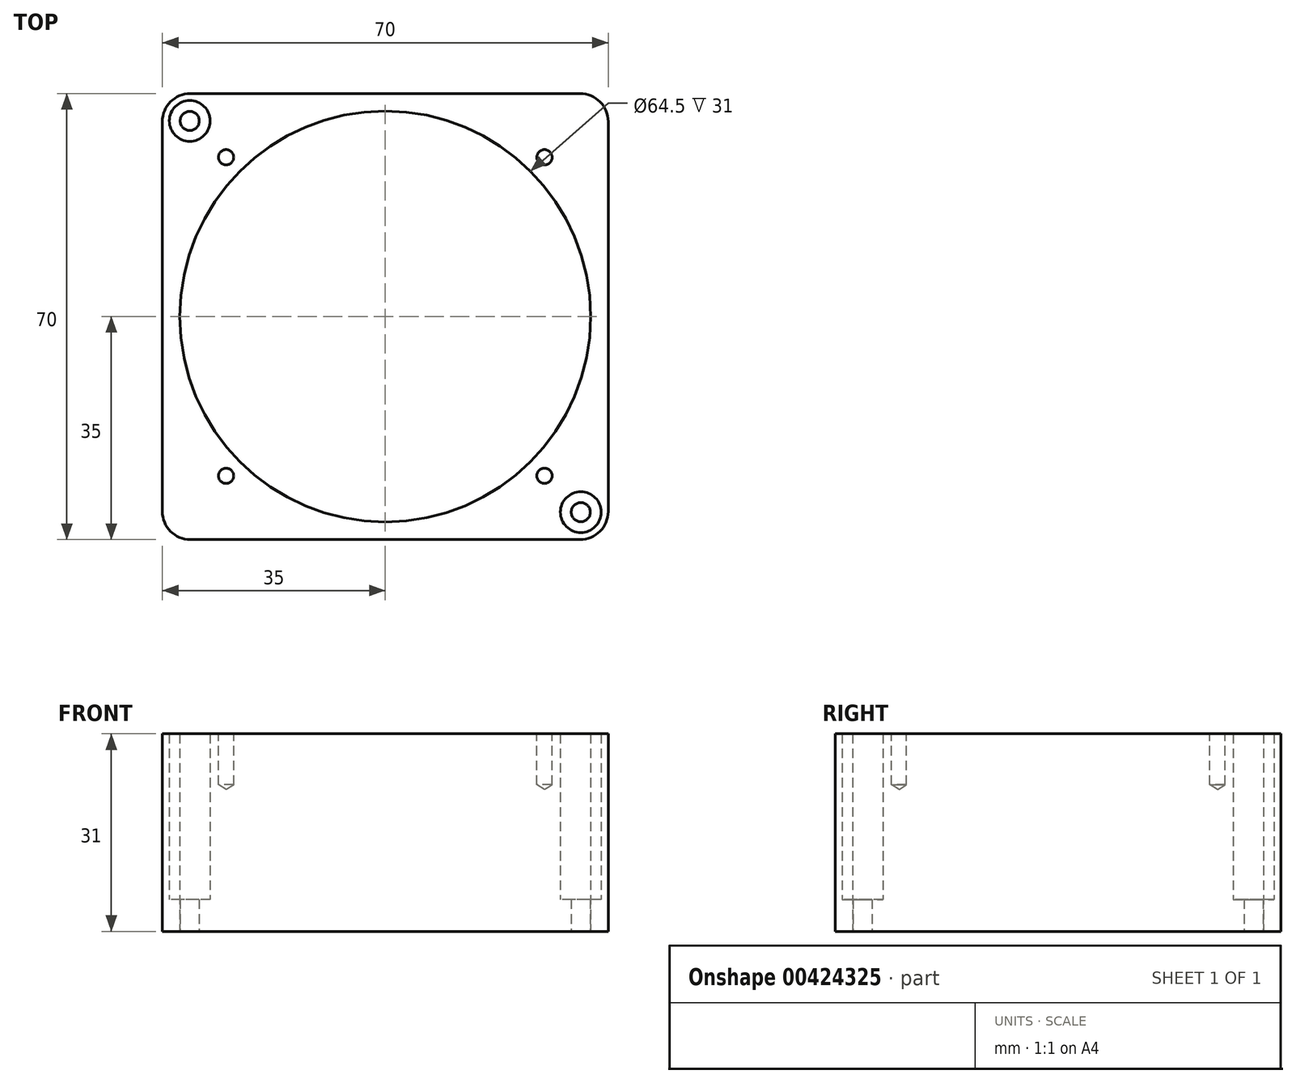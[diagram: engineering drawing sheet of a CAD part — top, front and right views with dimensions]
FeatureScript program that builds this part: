
annotation { "Feature Type Name" : "Feature", "Feature Type Description" : "" }
export const myFeature = defineFeature(function(context is Context, id is Id, definition is map)
    precondition{}
    {
        {
            var Q0;
            Q0=qCreatedBy(makeId("Top.planeOp"),FACE);
            var sketch = newSketch(context, id + "F0", { "sketchPlane" : qUnion([Q0])});
            skLineSegment(sketch, "E0.bottom", {"start": v(35, 35) * mm, "end": v(-35, 35) * mm});
            skLineSegment(sketch, "E0.top", {"start": v(35, -35) * mm, "end": v(-35, -35) * mm});
            skLineSegment(sketch, "E0.left", {"start": v(35, 35) * mm, "end": v(35, -35) * mm});
            skLineSegment(sketch, "E0.right", {"start": v(-35, 35) * mm, "end": v(-35, -35) * mm});
            skPoint(sketch, "E0.middle", {"position": v(0, 0) * mm});
            skCircle(sketch, "E1", {"center": v(0, 0) * mm, "radius": 32.25 * mm});
            skCircle(sketch, "E2", {"center": v(-30.7, 30.7) * mm, "radius": 3.2 * mm});
            skCircle(sketch, "E3", {"center": v(30.7, -30.7) * mm, "radius": 3.2 * mm});
            skCircle(sketch, "E4", {"center": v(-30.7, 30.7) * mm, "radius": 1.5 * mm});
            skCircle(sketch, "E5", {"center": v(30.7, -30.7) * mm, "radius": 1.5 * mm});
            skSolve(sketch);
        }
        {
            var Q0;
            {var subQ1=sQuery(id+"F0.wireOp",EDGE,"E0.top");Q0=makeQuery(id+"F0.imprint","IMPRINT",FACE,{"disambiguationData":[TD([[makeQuery(id+"F0.imprint","IMPRINT",EDGE,{"derivedFrom":subQ1}),-1.0]])]});}
            extrude(context, id + "F1", {"entities" : qUnion([Q0]), "depth" : 31 * mm});
        }
        {
            var Q0;
            Q0=makeQuery(id+"F0.imprint","IMPRINT",FACE,{"disambiguationData":[TD([[makeQuery(id+"F0.imprint","IMPRINT",EDGE,{"derivedFrom":sQuery(id+"F0.wireOp",EDGE,"E4")}),-1.0]])]});
            extrude(context, id + "F2", {"entities" : qUnion([Q0]), "operationType" : NewBodyOperationType.ADD, "depth" : 5 * mm});
        }
        {
            var Q0;
            Q0=makeQuery(id+"F0.imprint","IMPRINT",FACE,{"disambiguationData":[TD([[makeQuery(id+"F0.imprint","IMPRINT",EDGE,{"derivedFrom":sQuery(id+"F0.wireOp",EDGE,"E3")}),1.0]])]});
            extrude(context, id + "F3", {"entities" : qUnion([Q0]), "operationType" : NewBodyOperationType.ADD, "depth" : 5 * mm});
        }
        {
            var Q0;
            Q0=makeQuery(id+"F1.opExtrude","CAP_FACE",FACE,{"disambiguationData":[OSD([sQuery(id+"F0.wireOp",EDGE,"E0.bottom"),sQuery(id+"F0.wireOp",EDGE,"E0.top"),sQuery(id+"F0.wireOp",EDGE,"E0.left"),sQuery(id+"F0.wireOp",EDGE,"E0.right"),sQuery(id+"F0.wireOp",EDGE,"E1"),sQuery(id+"F0.wireOp",EDGE,"E2"),sQuery(id+"F0.wireOp",EDGE,"E3")])],"isStart":false});
            var sketch = newSketch(context, id + "F4", { "sketchPlane" : qUnion([Q0])});
            skPoint(sketch, "E6", {"position": v(-25, -25) * mm});
            skPoint(sketch, "E7", {"position": v(25, 25) * mm});
            skPoint(sketch, "E8", {"position": v(-25, 25) * mm});
            skPoint(sketch, "E9", {"position": v(25, -25) * mm});
            skSolve(sketch);
        }
        {
            var Q0;
            Q0=sQuery(id+"F4.wireOp",VERTEX,"E6");
            var Q1;
            Q1=sQuery(id+"F4.wireOp",VERTEX,"E7");
            var Q2;
            Q2=sQuery(id+"F4.wireOp",VERTEX,"E8");
            var Q3;
            Q3=sQuery(id+"F4.wireOp",VERTEX,"E9");
            var Q4;
            Q4=makeQuery(id+"F1.opExtrude","SWEPT_BODY",BODY,{"disambiguationData":[OSD([sQuery(id+"F0.wireOp",EDGE,"E0.bottom"),sQuery(id+"F0.wireOp",EDGE,"E0.top"),sQuery(id+"F0.wireOp",EDGE,"E0.left"),sQuery(id+"F0.wireOp",EDGE,"E0.right"),sQuery(id+"F0.wireOp",EDGE,"E1"),sQuery(id+"F0.wireOp",EDGE,"E2"),sQuery(id+"F0.wireOp",EDGE,"E3")])]});
            hole(context, id + "F5", {"style" : HoleStyle.SIMPLE, "endStyle" : HoleEndStyle.BLIND, "holeDiameter" : 2.4 * mm, "holeDepth" : 8 * mm, "isTappedThrough" : true, "tappedDepth" : 12 * mm, "tapClearance" : 3, "locations" : qUnion([Q0, Q1, Q2, Q3]), "scope" : qUnion([Q4])});
        }
        {
            var Q0;
            Q0=makeQuery(id+"F1.opExtrude","SWEPT_EDGE",EDGE,{"disambiguationData":[OSD([sQuery(id+"F0.wireOp",EDGE,"E0.top"),sQuery(id+"F0.wireOp",EDGE,"E0.right")])]});
            var Q1;
            Q1=makeQuery(id+"F1.opExtrude","SWEPT_EDGE",EDGE,{"disambiguationData":[OSD([sQuery(id+"F0.wireOp",EDGE,"E0.top"),sQuery(id+"F0.wireOp",EDGE,"E0.left")])]});
            var Q2;
            Q2=makeQuery(id+"F1.opExtrude","SWEPT_EDGE",EDGE,{"disambiguationData":[OSD([sQuery(id+"F0.wireOp",EDGE,"E0.bottom"),sQuery(id+"F0.wireOp",EDGE,"E0.left")])]});
            var Q3;
            Q3=makeQuery(id+"F1.opExtrude","SWEPT_EDGE",EDGE,{"disambiguationData":[OSD([sQuery(id+"F0.wireOp",EDGE,"E0.bottom"),sQuery(id+"F0.wireOp",EDGE,"E0.right")])]});
            fillet(context, id + "F6", {"entities" : qUnion([Q0, Q1, Q2, Q3]), "radius" : 4.4 * mm, "tangentPropagation" : true, "allowEdgeOverflow" : false});
        }
    });
